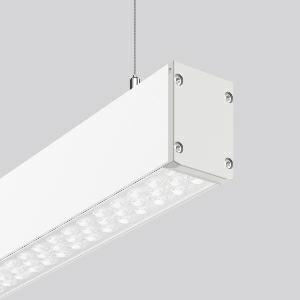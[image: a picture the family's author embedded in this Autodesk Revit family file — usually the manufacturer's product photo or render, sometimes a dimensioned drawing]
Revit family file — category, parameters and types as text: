
# Revit family: linedo_single_ip54_312565_002_1_76_f2cc
name_source: partatom
category: Lighting Fixtures
units: mm (PartAtom-declared; Revit-internal decimal feet)

## family parameters
Cut with Voids When Loaded = No
Host = Face
Light Source = No
Part Type = Normal
Room Calculation Point = No
Round Connector Dimension = Use Diameter
Shared = No

## types (1)
- LINEDO single IP54 (1 x LED Modul 840, 4850 lm, 4000)
    Apparent Load = 31 VA
    CIE Flux Codes = 86 96 99 100 100
    Color Rendering = 80
    Color Temperature = 4000
    Default Elevation = 1800 mm
    Description = Series: LINEDO single IP54
Stylish pendant luminaire. Housing: extruded aluminium profile, powder-coated. Plastic end caps, grey. High-efficiency LED units with optimum light control thanks to clear plastic (PC) lens optics. 2-point steel cable suspension freely positionable and infinitely height-adjustable. With power cord (2.5 m). Please order canopy separately if required. Perfect for office areas (RUG < 19) and environments with computer screens in accordance with EN 12464-1. Luminaire with limited surface temperature in accordance with EN 60598-2-24 for use in environments in which a deposit of conductive dust on the luminaire can be expected. 
Colour: traffic white, matt (RAL 9016)
Length: 1710 mm
Width: 58 mm
Height: 76 mm
Suspension length: 100-1500 mm
Lamp: LED
Socket: without socket
Colour temperature: 4000K
Colour rendering index (CRI): 80
System power: 31 W
Rated luminous flux: 4850 lm
Beam angle Down: 59°
Luminous efficiency: 156 lm/W
Control gear: Converter, dimmable, DALI
Protection class: I
Type of protection: IP 54
    Height = 76 mm
    Lamp = 1 x LED Modul 840
    Lamp Light Flux = 4850 lm
    Lamp count = 1
    Length = 1710 mm
    Lifetime = 50000 h
    Luminous efficacy = 156 lm/W
    Manufacturer = RZB
    ModVariant = No
    Model = 312565.002.1.76
    Mounting Place = Ceiling
    Mounting Type = Surface mounted, Pendant
    Number of Poles = 1
    OnlyDefault = Yes
    Power Factor = 1
    Product Name = LINEDO single IP54
    Product group = Pendant luminaires
    ProductGroupID = 902
    Protection Class = Protection class I
    Protection Degree = IP 54
    RLX_Detail_Level = 1
    RLX_Emergency_Light_Flux = 0 lm
    RLX_Emergency_Type = 0
    RLX_Emergency_Type_DB = No
    RlxData = <blob elided: 27017 chars, md5=e3f5d330>
    Socket = socket
    Standby Power = 0 W
    System Light Flux = 4850 lm
    System Power = 31 W
    Type Comments = ALEA SPOT
    Type Image = 312565.002.jpg
    URL = http://relux.com
    VarID = ---
    Voltage = 230 V
    Voltage Range = 220-240 V
    Weight = 0.00 kg
    Width = 58 mm

## geometry (parser evidence)
native form markers: Blend x4, Sweep x13
no freeform markers — native parametric forms only
